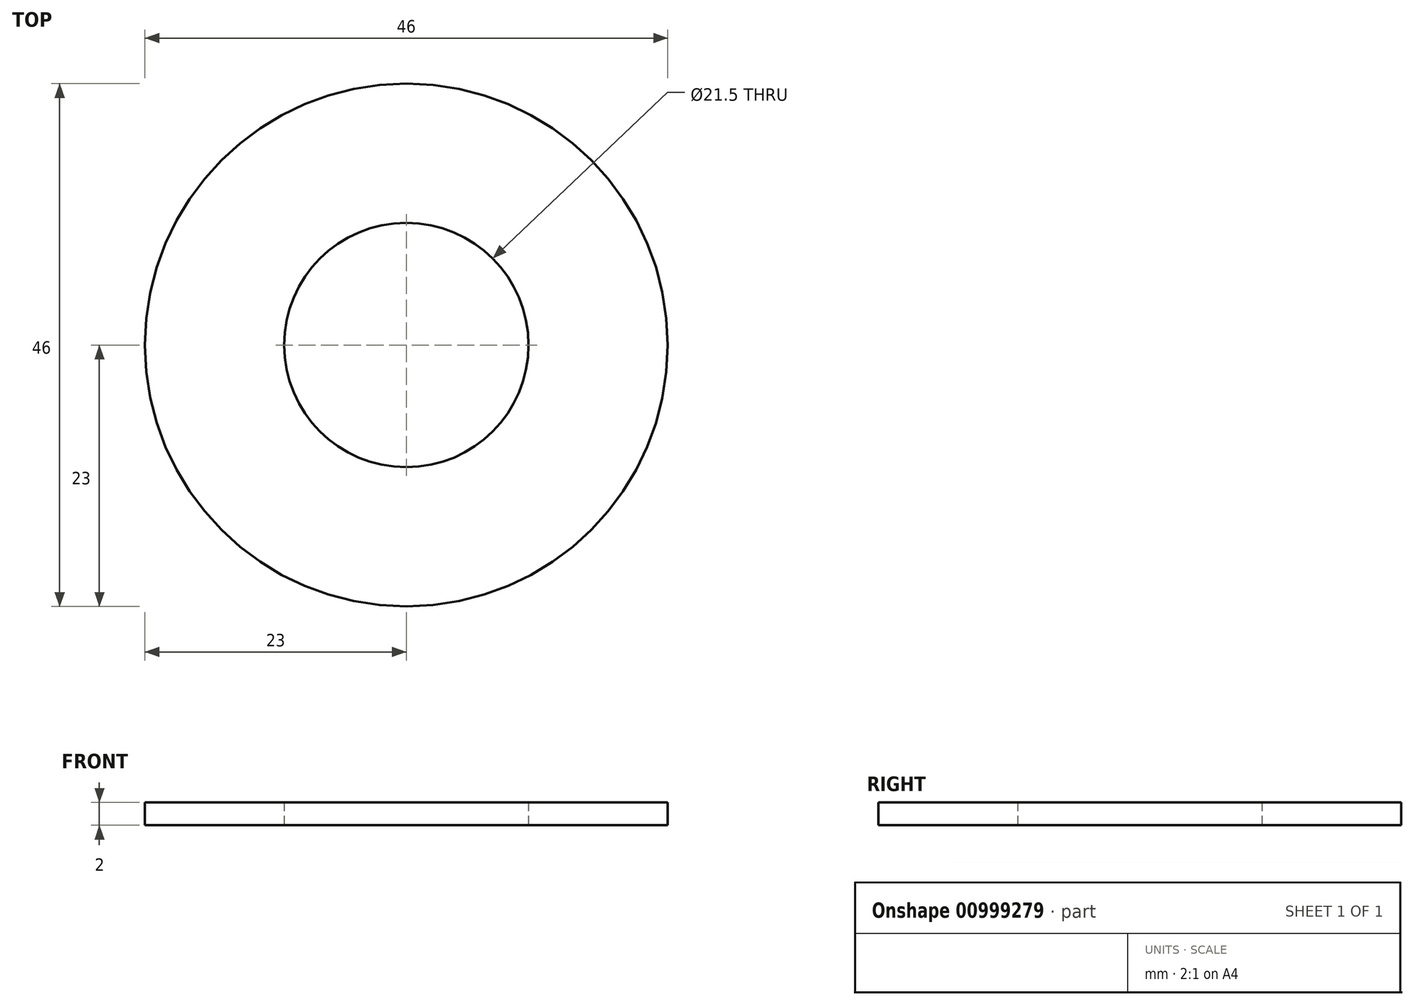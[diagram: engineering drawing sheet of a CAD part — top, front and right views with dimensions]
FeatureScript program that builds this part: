
annotation { "Feature Type Name" : "Feature", "Feature Type Description" : "" }
export const myFeature = defineFeature(function(context is Context, id is Id, definition is map)
    precondition{}
    {
        {
            var Q0;
            Q0=qCreatedBy(makeId("Top.planeOp"),FACE);
            var sketch = newSketch(context, id + "F0", { "sketchPlane" : qUnion([Q0])});
            skCircle(sketch, "E0", {"center": v(0, 0) * mm, "radius": 10.75 * mm});
            skCircle(sketch, "E1", {"center": v(0, 0) * mm, "radius": 23 * mm});
            skSolve(sketch);
        }
        {
            var Q0;
            Q0=makeQuery(id+"F0.imprint","IMPRINT",FACE,{"disambiguationData":[TD([[makeQuery(id+"F0.imprint","IMPRINT",EDGE,{"derivedFrom":sQuery(id+"F0.wireOp",EDGE,"E0")}),-1.0]])]});
            extrude(context, id + "F1", {"entities" : qUnion([Q0]), "depth" : 2 * mm, "offsetDistance" : 25 * mm});
        }
    });
